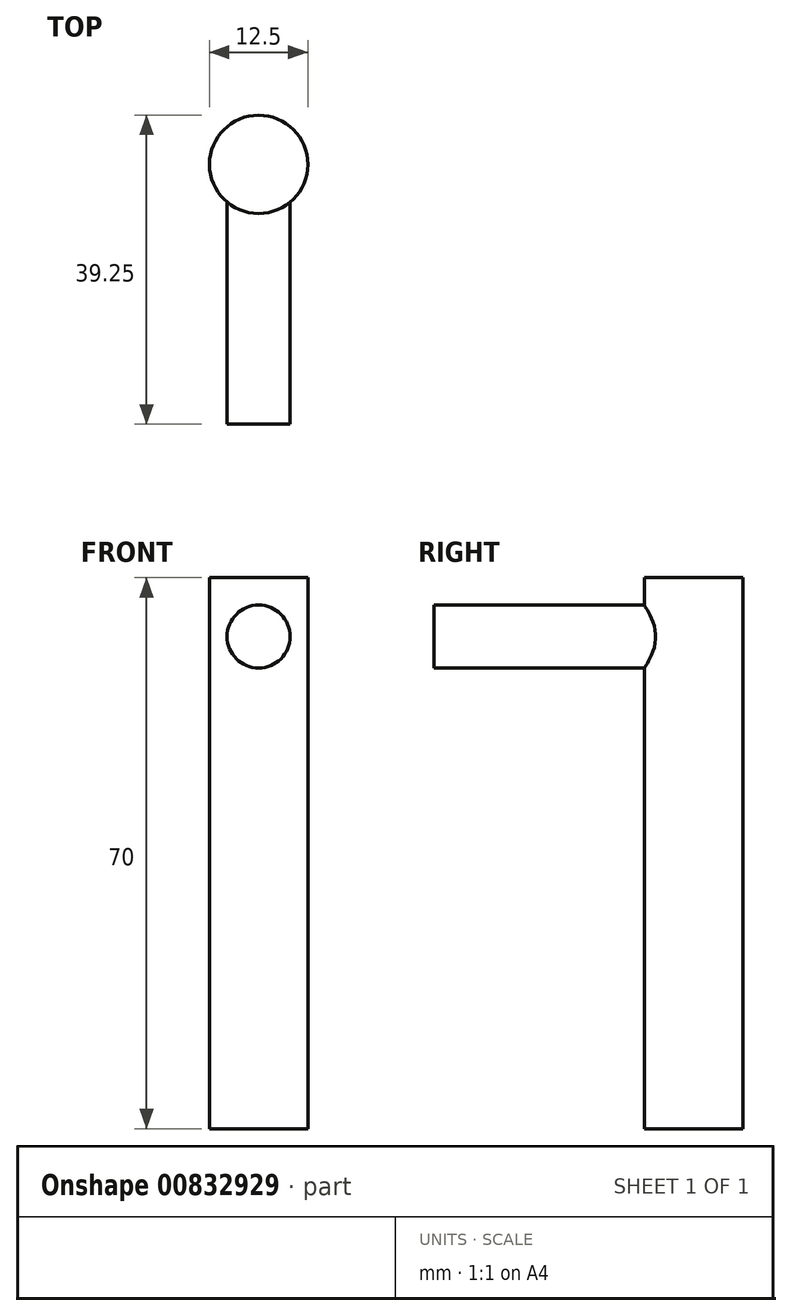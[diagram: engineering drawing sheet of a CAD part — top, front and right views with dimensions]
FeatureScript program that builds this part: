
annotation { "Feature Type Name" : "Feature", "Feature Type Description" : "" }
export const myFeature = defineFeature(function(context is Context, id is Id, definition is map)
    precondition{}
    {
        {
            var Q0;
            Q0=qCreatedBy(makeId("Front.planeOp"),FACE);
            var sketch = newSketch(context, id + "F0", { "sketchPlane" : qUnion([Q0])});
            skCircle(sketch, "E0", {"center": v(0, 22.52) * mm, "radius": 4 * mm});
            skSolve(sketch);
        }
        {
            var Q0;
            Q0=qCreatedBy(makeId("Top.planeOp"),FACE);
            var sketch = newSketch(context, id + "F1", { "sketchPlane" : qUnion([Q0])});
            skCircle(sketch, "E1", {"center": v(0, 33) * mm, "radius": 6.25 * mm});
            skSolve(sketch);
        }
        {
            var Q0;
            Q0=makeQuery(id+"F1.imprint","IMPRINT",FACE,{"disambiguationData":[TD([[makeQuery(id+"F1.imprint","IMPRINT",EDGE,{"derivedFrom":sQuery(id+"F1.wireOp",EDGE,"E1")}),1.0]])]});
            extrude(context, id + "F2", {"entities" : qUnion([Q0]), "depth" : 30 * mm, "offsetDistance" : 25 * mm, "hasSecondDirection" : true, "secondDirectionOppositeDirection" : true, "secondDirectionDepth" : 40 * mm});
        }
        {
            var Q0;
            Q0=makeQuery(id+"F0.imprint","IMPRINT",FACE,{"disambiguationData":[TD([[makeQuery(id+"F0.imprint","IMPRINT",EDGE,{"derivedFrom":sQuery(id+"F0.wireOp",EDGE,"E0")}),1.0]])]});
            extrude(context, id + "F3", {"entities" : qUnion([Q0]), "operationType" : NewBodyOperationType.ADD, "endBound" : BoundingType.UP_TO_NEXT, "oppositeDirection" : true, "depth" : 25 * mm, "offsetDistance" : 25 * mm});
        }
    });
